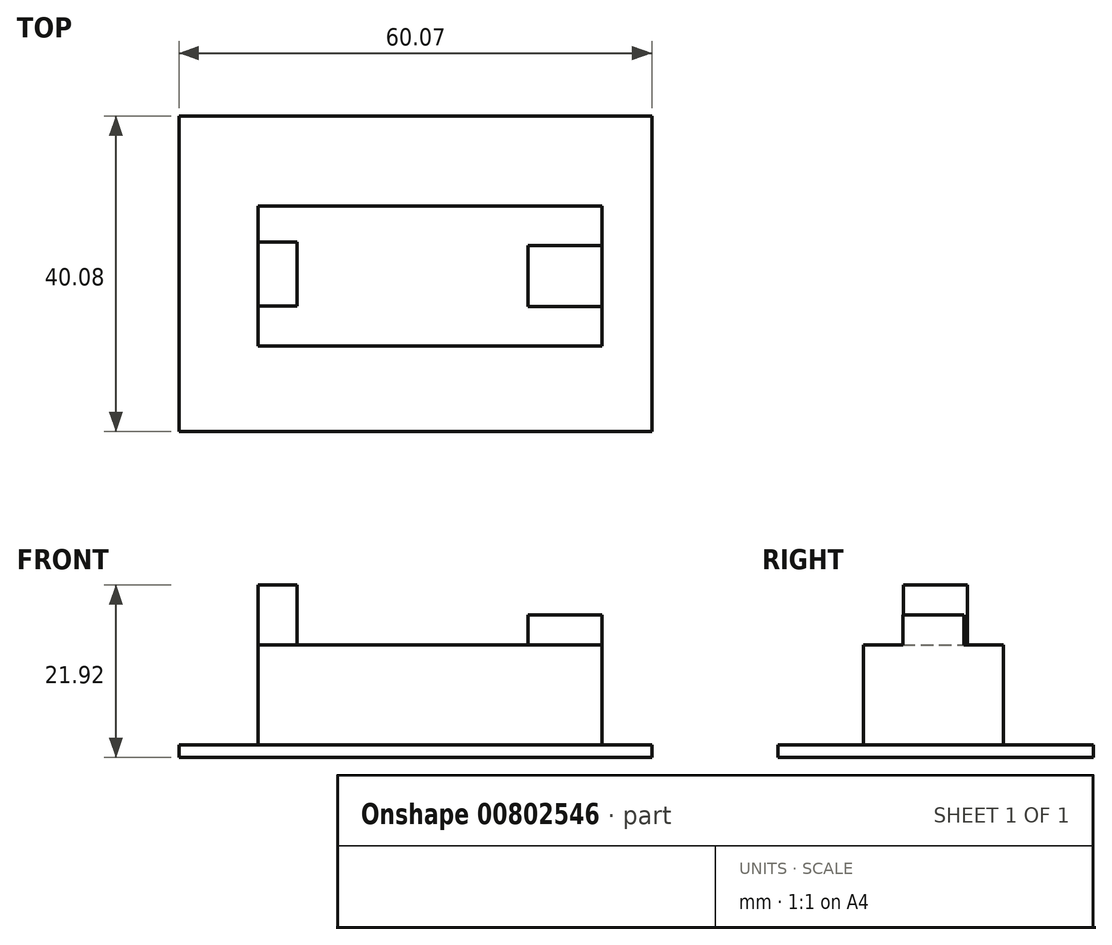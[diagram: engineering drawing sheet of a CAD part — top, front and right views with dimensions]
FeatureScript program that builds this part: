
annotation { "Feature Type Name" : "Feature", "Feature Type Description" : "" }
export const myFeature = defineFeature(function(context is Context, id is Id, definition is map)
    precondition{}
    {
        {
            var Q0;
            Q0=qCreatedBy(makeId("Top.planeOp"),FACE);
            var sketch = newSketch(context, id + "F0", { "sketchPlane" : qUnion([Q0])});
            skLineSegment(sketch, "E0", {"start": v(-60.07, 40.08) * mm, "end": v(-60.07, 0) * mm});
            skLineSegment(sketch, "E1", {"start": v(-60.07, 0) * mm, "end": v(0, 0) * mm});
            skLineSegment(sketch, "E2", {"start": v(0, 0) * mm, "end": v(0, 40.08) * mm});
            skLineSegment(sketch, "E3", {"start": v(0, 40.08) * mm, "end": v(-60.07, 40.08) * mm});
            skSolve(sketch);
        }
        {
            var Q0;
            Q0=makeQuery(id+"F0.imprint","IMPRINT",FACE,{"disambiguationData":[TD([[makeQuery(id+"F0.imprint","IMPRINT",EDGE,{"derivedFrom":sQuery(id+"F0.wireOp",EDGE,"E0")}),1.0]])]});
            extrude(context, id + "F1", {"entities" : qUnion([Q0]), "depth" : 1.6 * mm, "offsetDistance" : 25.4 * mm});
        }
        {
            var Q0;
            Q0=makeQuery(id+"F1.opExtrude","CAP_FACE",FACE,{"disambiguationData":[OSD([sQuery(id+"F0.wireOp",EDGE,"E0"),sQuery(id+"F0.wireOp",EDGE,"E1"),sQuery(id+"F0.wireOp",EDGE,"E2"),sQuery(id+"F0.wireOp",EDGE,"E3")])],"isStart":false});
            var sketch = newSketch(context, id + "F2", { "sketchPlane" : qUnion([Q0])});
            skLineSegment(sketch, "E4", {"start": v(-6.35, 28.65) * mm, "end": v(-50.01, 28.65) * mm});
            skLineSegment(sketch, "E5", {"start": v(-50.01, 28.65) * mm, "end": v(-50.01, 10.87) * mm});
            skLineSegment(sketch, "E6", {"start": v(-50.01, 10.87) * mm, "end": v(-6.35, 10.87) * mm});
            skLineSegment(sketch, "E7", {"start": v(-6.35, 10.87) * mm, "end": v(-6.35, 28.65) * mm});
            skSolve(sketch);
        }
        {
            var Q0;
            Q0=makeQuery(id+"F2.imprint","IMPRINT",FACE,{"disambiguationData":[TD([[makeQuery(id+"F2.imprint","IMPRINT",EDGE,{"derivedFrom":sQuery(id+"F2.wireOp",EDGE,"E4")}),1.0]])]});
            extrude(context, id + "F3", {"entities" : qUnion([Q0]), "operationType" : NewBodyOperationType.ADD, "depth" : 12.7 * mm, "offsetDistance" : 25.4 * mm});
        }
        {
            var Q0;
            Q0=makeQuery(id+"F3.opExtrude","CAP_FACE",FACE,{"disambiguationData":[OSD([sQuery(id+"F2.wireOp",EDGE,"E4"),sQuery(id+"F2.wireOp",EDGE,"E5"),sQuery(id+"F2.wireOp",EDGE,"E6"),sQuery(id+"F2.wireOp",EDGE,"E7")])],"isStart":false});
            var sketch = newSketch(context, id + "F4", { "sketchPlane" : qUnion([Q0])});
            skLineSegment(sketch, "E8", {"start": v(-50.01, 15.95) * mm, "end": v(-45.09, 15.95) * mm});
            skLineSegment(sketch, "E9", {"start": v(-45.09, 15.95) * mm, "end": v(-45.09, 24.08) * mm});
            skLineSegment(sketch, "E10", {"start": v(-45.09, 24.08) * mm, "end": v(-50.01, 24.08) * mm});
            skLineSegment(sketch, "E11", {"start": v(-6.35, 19.76) * mm, "end": v(-15.33, 19.76) * mm, "construction": true});
            skLineSegment(sketch, "E12", {"start": v(-6.35, 15.9) * mm, "end": v(-15.72, 15.9) * mm});
            skLineSegment(sketch, "E13.MirrorCS", {"start": v(-6.35, 23.62) * mm, "end": v(-15.72, 23.62) * mm});
            skLineSegment(sketch, "E14", {"start": v(-15.72, 15.9) * mm, "end": v(-15.72, 23.62) * mm});
            skSolve(sketch);
        }
        {
            var Q0;
            {var subQ0=sQuery(id+"F4.wireOp",EDGE,"E12");Q0=makeQuery(id+"F4.imprint","IMPRINT",FACE,{"disambiguationData":[TD([[makeQuery(id+"F4.imprint","IMPRINT",EDGE,{"derivedFrom":subQ0}),-1.0]])]});}
            extrude(context, id + "F5", {"entities" : qUnion([Q0]), "operationType" : NewBodyOperationType.ADD, "depth" : 3.8 * mm, "offsetDistance" : 25.4 * mm});
        }
        {
            var Q0;
            {var subQ0=sQuery(id+"F4.wireOp",EDGE,"E8");Q0=makeQuery(id+"F4.imprint","IMPRINT",FACE,{"disambiguationData":[TD([[makeQuery(id+"F4.imprint","IMPRINT",EDGE,{"derivedFrom":subQ0}),1.0]])]});}
            extrude(context, id + "F6", {"entities" : qUnion([Q0]), "operationType" : NewBodyOperationType.ADD, "depth" : 7.62 * mm, "offsetDistance" : 25.4 * mm});
        }
    });
